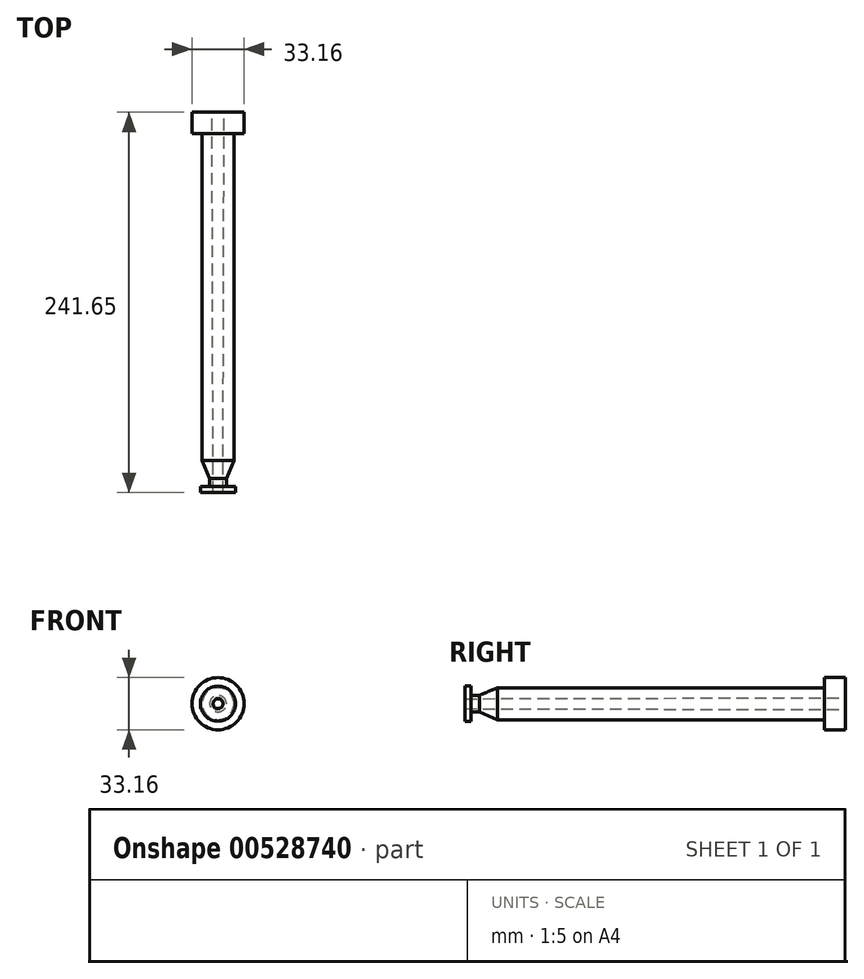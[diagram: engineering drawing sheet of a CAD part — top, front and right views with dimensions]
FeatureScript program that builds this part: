
annotation { "Feature Type Name" : "Feature", "Feature Type Description" : "" }
export const myFeature = defineFeature(function(context is Context, id is Id, definition is map)
    precondition{}
    {
        {
            var Q0;
            Q0=qCreatedBy(makeId("Right.planeOp"),FACE);
            var sketch = newSketch(context, id + "F0", { "sketchPlane" : qUnion([Q0])});
            skLineSegment(sketch, "E0", {"start": v(-43.88, 3.14) * mm, "end": v(-43.88, 11.16) * mm});
            skLineSegment(sketch, "E1", {"start": v(-43.88, 11.16) * mm, "end": v(-40.08, 11.16) * mm});
            skLineSegment(sketch, "E2", {"start": v(-40.08, 11.16) * mm, "end": v(-40.08, 5.3) * mm});
            skLineSegment(sketch, "E3", {"start": v(-40.08, 5.3) * mm, "end": v(-34.84, 5.3) * mm});
            skLineSegment(sketch, "E4", {"start": v(-34.84, 5.3) * mm, "end": v(-23.39, 10.15) * mm});
            skLineSegment(sketch, "E5", {"start": v(-23.39, 10.15) * mm, "end": v(184.22, 10.15) * mm});
            skLineSegment(sketch, "E6", {"start": v(197.77, 10.15) * mm, "end": v(197.77, 3.8) * mm});
            skLineSegment(sketch, "E7", {"start": v(197.77, 3.8) * mm, "end": v(-43.88, 3.14) * mm});
            skLineSegment(sketch, "E8", {"start": v(184.22, 10.15) * mm, "end": v(184.22, 16.58) * mm});
            skLineSegment(sketch, "E9", {"start": v(184.22, 16.58) * mm, "end": v(197.77, 16.58) * mm});
            skLineSegment(sketch, "E10", {"start": v(197.77, 16.58) * mm, "end": v(197.77, 10.15) * mm});
            skLineSegment(sketch, "E11", {"start": v(0, 0) * mm, "end": v(-91.5, 0) * mm, "construction": true});
            skSolve(sketch);
        }
        {
            var Q0;
            Q0=makeQuery(id+"F0.imprint","IMPRINT",FACE,{"disambiguationData":[TD([[makeQuery(id+"F0.imprint","IMPRINT",EDGE,{"derivedFrom":sQuery(id+"F0.wireOp",EDGE,"E0")}),-1.0]])]});
            var Q1;
            Q1=sQuery(id+"F0.wireOp",EDGE,"E11");
            revolve(context, id + "F1", {"entities" : qUnion([Q0]), "axis" : qUnion([Q1]), "revolveType" : RevolveType.FULL});
        }
    });
